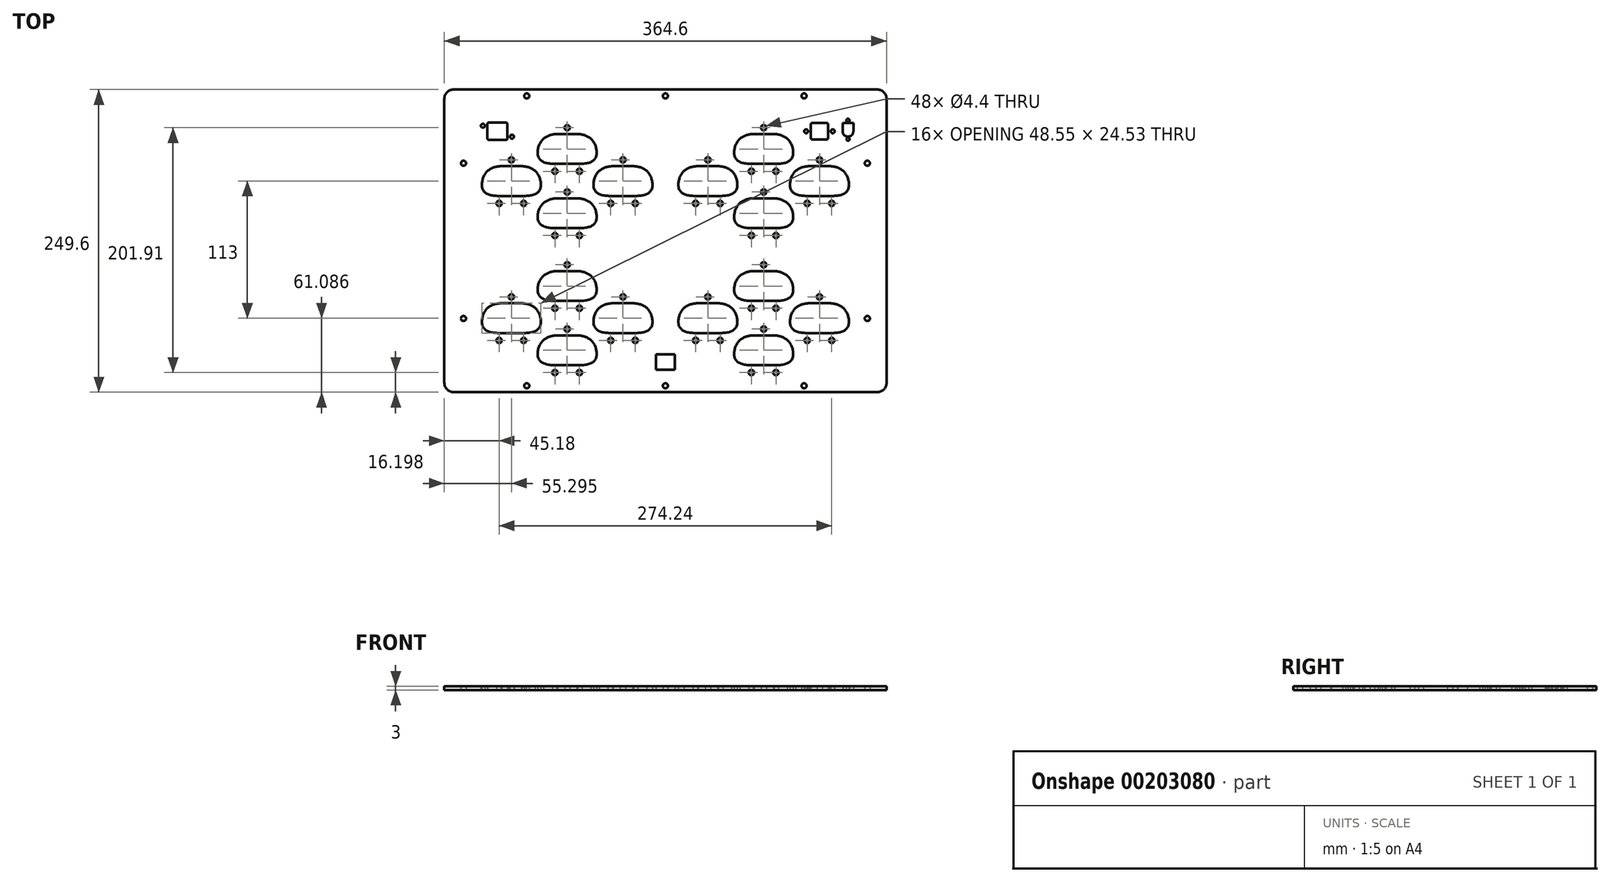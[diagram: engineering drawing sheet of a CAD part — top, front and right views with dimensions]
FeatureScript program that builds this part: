
annotation { "Feature Type Name" : "Feature", "Feature Type Description" : "" }
export const myFeature = defineFeature(function(context is Context, id is Id, definition is map)
    precondition{}
    {
        {
            var Q0;
            Q0=qCreatedBy(makeId("Top.planeOp"),FACE);
            var sketch = newSketch(context, id + "F0", { "sketchPlane" : qUnion([Q0])});
            skLineSegment(sketch, "E0.bottom", {"start": v(-174.5, 124.8) * mm, "end": v(174.5, 124.8) * mm});
            skLineSegment(sketch, "E0.top", {"start": v(-174.5, -124.8) * mm, "end": v(174.5, -124.8) * mm});
            skLineSegment(sketch, "E0.left", {"start": v(-182.3, 117) * mm, "end": v(-182.3, -117) * mm});
            skLineSegment(sketch, "E0.right", {"start": v(182.3, 117) * mm, "end": v(182.3, -117) * mm});
            skPoint(sketch, "E1.visualSharp", {"position": v(-182.3, 124.8) * mm});
            skArc(sketch, "E1.filletArc", {"start": v(-174.5, 124.8) * mm, "mid": v(-180.02, 122.52) * mm, "end": v(-182.3, 117) * mm});
            skPoint(sketch, "E2.visualSharp", {"position": v(182.3, 124.8) * mm});
            skArc(sketch, "E2.filletArc", {"start": v(182.3, 117) * mm, "mid": v(180.02, 122.52) * mm, "end": v(174.5, 124.8) * mm});
            skPoint(sketch, "E3.visualSharp", {"position": v(182.3, -124.8) * mm});
            skArc(sketch, "E3.filletArc", {"start": v(174.5, -124.8) * mm, "mid": v(180.02, -122.52) * mm, "end": v(182.3, -117) * mm});
            skPoint(sketch, "E4.visualSharp", {"position": v(-182.3, -124.8) * mm});
            skArc(sketch, "E4.filletArc", {"start": v(-182.3, -117) * mm, "mid": v(-180.02, -122.52) * mm, "end": v(-174.5, -124.8) * mm});
            skCircle(sketch, "E5", {"center": v(-166.5, -64) * mm, "radius": 2.1 * mm});
            skCircle(sketch, "E6", {"center": v(-166.5, 64) * mm, "radius": 2.1 * mm});
            skCircle(sketch, "E7.MirrorC", {"center": v(166.5, 64) * mm, "radius": 2.1 * mm});
            skCircle(sketch, "E8.MirrorC", {"center": v(166.5, -64) * mm, "radius": 2.1 * mm});
            skCircle(sketch, "E9", {"center": v(-114.33, -119.5) * mm, "radius": 2.1 * mm});
            skCircle(sketch, "E10", {"center": v(0, -119.5) * mm, "radius": 2.1 * mm});
            skCircle(sketch, "E11.MirrorC", {"center": v(114.33, -119.5) * mm, "radius": 2.1 * mm});
            skCircle(sketch, "E12.MirrorC", {"center": v(-114.33, 119.5) * mm, "radius": 2.1 * mm});
            skCircle(sketch, "E13.MirrorC", {"center": v(0, 119.5) * mm, "radius": 2.1 * mm});
            skCircle(sketch, "E14.MirrorC", {"center": v(114.33, 119.5) * mm, "radius": 2.1 * mm});
            skLineSegment(sketch, "E15.1", {"start": v(-135.12, -51.46) * mm, "end": v(-118.9, -51.46) * mm});
            skLineSegment(sketch, "E15.3", {"start": v(-118.9, -51.46) * mm, "end": v(-118.33, -51.45) * mm});
            skArc(sketch, "E15.4", {"start": v(-118.33, -51.45) * mm, "mid": v(-112.6, -52.41) * mm, "end": v(-107.49, -55.2) * mm});
            skArc(sketch, "E15.5", {"start": v(-107.49, -55.2) * mm, "mid": v(-103.73, -60.96) * mm, "end": v(-102.78, -67.78) * mm});
            skLineSegment(sketch, "E15.8", {"start": v(-135.1, -75.97) * mm, "end": v(-118.9, -75.97) * mm});
            skFitSpline(sketch, "E15.9", {"points": [v(-102.78, -67.78) * mm, v(-102.83, -68.48) * mm, v(-103.13, -69.85) * mm, v(-104.12, -71.74) * mm, v(-105.36, -73.07) * mm, v(-106.59, -73.94) * mm, v(-107.95, -74.65) * mm, v(-109.89, -75.3) * mm, v(-112.56, -75.75) * mm, v(-115.56, -75.96) * mm, v(-117.76, -75.98) * mm, v(-118.9, -75.97) * mm]});
            skCircle(sketch, "E16", {"center": v(-127, -46.2) * mm, "radius": 2.2 * mm});
            skCircle(sketch, "E17", {"center": v(-137.12, -82.1) * mm, "radius": 2.2 * mm});
            skCircle(sketch, "E18", {"center": v(-116.88, -82.1) * mm, "radius": 2.2 * mm});
            skFitSpline(sketch, "E19.0", {"points": [v(-151.23, -67.78) * mm, v(-151.18, -68.48) * mm, v(-150.87, -69.85) * mm, v(-149.88, -71.74) * mm, v(-148.63, -73.07) * mm, v(-147.4, -73.93) * mm, v(-146.05, -74.65) * mm, v(-144.11, -75.3) * mm, v(-141.44, -75.75) * mm, v(-138.45, -75.95) * mm, v(-136.25, -75.98) * mm, v(-135.1, -75.97) * mm]});
            skArc(sketch, "E19.1", {"start": v(-146.52, -55.2) * mm, "mid": v(-150.28, -60.96) * mm, "end": v(-151.23, -67.78) * mm});
            skArc(sketch, "E19.2", {"start": v(-135.66, -51.45) * mm, "mid": v(-141.4, -52.41) * mm, "end": v(-146.52, -55.2) * mm});
            skLineSegment(sketch, "E20.0", {"start": v(-135.1, -51.46) * mm, "end": v(-135.66, -51.45) * mm});
            skPoint(sketch, "E21", {"position": v(-156, -112.5) * mm});
            skLineSegment(sketch, "E22.1", {"start": v(-89.12, -77.96) * mm, "end": v(-72.9, -77.96) * mm});
            skLineSegment(sketch, "E22.3", {"start": v(-72.9, -77.96) * mm, "end": v(-72.33, -77.95) * mm});
            skArc(sketch, "E22.4", {"start": v(-72.33, -77.95) * mm, "mid": v(-66.6, -78.91) * mm, "end": v(-61.49, -81.7) * mm});
            skArc(sketch, "E22.5", {"start": v(-61.49, -81.7) * mm, "mid": v(-57.73, -87.46) * mm, "end": v(-56.78, -94.28) * mm});
            skLineSegment(sketch, "E22.8", {"start": v(-89.1, -102.47) * mm, "end": v(-72.9, -102.47) * mm});
            skFitSpline(sketch, "E22.9", {"points": [v(-56.78, -94.28) * mm, v(-56.83, -94.98) * mm, v(-57.13, -96.35) * mm, v(-58.12, -98.24) * mm, v(-59.36, -99.57) * mm, v(-60.58, -100.44) * mm, v(-61.95, -101.15) * mm, v(-63.88, -101.8) * mm, v(-66.56, -102.25) * mm, v(-69.56, -102.45) * mm, v(-71.76, -102.48) * mm, v(-72.9, -102.47) * mm]});
            skCircle(sketch, "E23", {"center": v(-81, -72.7) * mm, "radius": 2.2 * mm});
            skCircle(sketch, "E24", {"center": v(-91.12, -108.6) * mm, "radius": 2.2 * mm});
            skCircle(sketch, "E25", {"center": v(-70.88, -108.6) * mm, "radius": 2.2 * mm});
            skFitSpline(sketch, "E26.0", {"points": [v(-105.23, -94.28) * mm, v(-105.18, -94.98) * mm, v(-104.87, -96.35) * mm, v(-103.88, -98.24) * mm, v(-102.63, -99.57) * mm, v(-101.4, -100.43) * mm, v(-100.05, -101.15) * mm, v(-98.11, -101.8) * mm, v(-95.44, -102.25) * mm, v(-92.45, -102.45) * mm, v(-90.25, -102.48) * mm, v(-89.1, -102.47) * mm]});
            skArc(sketch, "E26.1", {"start": v(-100.52, -81.7) * mm, "mid": v(-104.28, -87.46) * mm, "end": v(-105.23, -94.28) * mm});
            skArc(sketch, "E26.2", {"start": v(-89.66, -77.95) * mm, "mid": v(-95.4, -78.91) * mm, "end": v(-100.52, -81.7) * mm});
            skLineSegment(sketch, "E27.0", {"start": v(-89.1, -77.96) * mm, "end": v(-89.66, -77.95) * mm});
            skLineSegment(sketch, "E28.1", {"start": v(-43.12, -51.46) * mm, "end": v(-26.9, -51.46) * mm});
            skLineSegment(sketch, "E28.3", {"start": v(-26.9, -51.46) * mm, "end": v(-26.33, -51.45) * mm});
            skArc(sketch, "E28.4", {"start": v(-26.33, -51.45) * mm, "mid": v(-20.6, -52.41) * mm, "end": v(-15.49, -55.2) * mm});
            skArc(sketch, "E28.5", {"start": v(-15.49, -55.2) * mm, "mid": v(-11.73, -60.96) * mm, "end": v(-10.78, -67.78) * mm});
            skLineSegment(sketch, "E28.8", {"start": v(-43.1, -75.97) * mm, "end": v(-26.9, -75.97) * mm});
            skFitSpline(sketch, "E28.9", {"points": [v(-10.78, -67.78) * mm, v(-10.83, -68.48) * mm, v(-11.13, -69.85) * mm, v(-12.12, -71.74) * mm, v(-13.36, -73.07) * mm, v(-14.59, -73.94) * mm, v(-15.95, -74.65) * mm, v(-17.89, -75.3) * mm, v(-20.56, -75.75) * mm, v(-23.56, -75.96) * mm, v(-25.76, -75.98) * mm, v(-26.9, -75.97) * mm]});
            skCircle(sketch, "E29", {"center": v(-35, -46.2) * mm, "radius": 2.2 * mm});
            skCircle(sketch, "E30", {"center": v(-45.12, -82.1) * mm, "radius": 2.2 * mm});
            skCircle(sketch, "E31", {"center": v(-24.88, -82.1) * mm, "radius": 2.2 * mm});
            skFitSpline(sketch, "E32.0", {"points": [v(-59.23, -67.78) * mm, v(-59.18, -68.48) * mm, v(-58.87, -69.85) * mm, v(-57.88, -71.74) * mm, v(-56.63, -73.07) * mm, v(-55.4, -73.93) * mm, v(-54.05, -74.65) * mm, v(-52.11, -75.3) * mm, v(-49.44, -75.75) * mm, v(-46.45, -75.95) * mm, v(-44.25, -75.98) * mm, v(-43.1, -75.97) * mm]});
            skArc(sketch, "E32.1", {"start": v(-54.52, -55.2) * mm, "mid": v(-58.28, -60.96) * mm, "end": v(-59.23, -67.78) * mm});
            skArc(sketch, "E32.2", {"start": v(-43.66, -51.45) * mm, "mid": v(-49.4, -52.41) * mm, "end": v(-54.52, -55.2) * mm});
            skLineSegment(sketch, "E33.0", {"start": v(-43.1, -51.46) * mm, "end": v(-43.66, -51.45) * mm});
            skLineSegment(sketch, "E34.1", {"start": v(-89.12, -24.96) * mm, "end": v(-72.9, -24.96) * mm});
            skLineSegment(sketch, "E34.3", {"start": v(-72.9, -24.96) * mm, "end": v(-72.33, -24.95) * mm});
            skArc(sketch, "E34.4", {"start": v(-72.33, -24.95) * mm, "mid": v(-66.6, -25.91) * mm, "end": v(-61.49, -28.7) * mm});
            skArc(sketch, "E34.5", {"start": v(-61.49, -28.7) * mm, "mid": v(-57.73, -34.46) * mm, "end": v(-56.78, -41.28) * mm});
            skLineSegment(sketch, "E34.8", {"start": v(-89.1, -49.47) * mm, "end": v(-72.9, -49.47) * mm});
            skFitSpline(sketch, "E34.9", {"points": [v(-56.78, -41.28) * mm, v(-56.83, -41.98) * mm, v(-57.13, -43.35) * mm, v(-58.12, -45.24) * mm, v(-59.36, -46.57) * mm, v(-60.59, -47.44) * mm, v(-61.95, -48.15) * mm, v(-63.89, -48.8) * mm, v(-66.56, -49.25) * mm, v(-69.56, -49.46) * mm, v(-71.76, -49.48) * mm, v(-72.9, -49.47) * mm]});
            skCircle(sketch, "E35", {"center": v(-81, -19.7) * mm, "radius": 2.2 * mm});
            skCircle(sketch, "E36", {"center": v(-91.12, -55.6) * mm, "radius": 2.2 * mm});
            skCircle(sketch, "E37", {"center": v(-70.88, -55.6) * mm, "radius": 2.2 * mm});
            skFitSpline(sketch, "E38.0", {"points": [v(-105.23, -41.28) * mm, v(-105.18, -41.98) * mm, v(-104.87, -43.35) * mm, v(-103.88, -45.24) * mm, v(-102.63, -46.57) * mm, v(-101.4, -47.43) * mm, v(-100.05, -48.15) * mm, v(-98.11, -48.8) * mm, v(-95.44, -49.25) * mm, v(-92.45, -49.45) * mm, v(-90.25, -49.48) * mm, v(-89.1, -49.47) * mm]});
            skArc(sketch, "E38.1", {"start": v(-100.52, -28.7) * mm, "mid": v(-104.28, -34.46) * mm, "end": v(-105.23, -41.28) * mm});
            skArc(sketch, "E38.2", {"start": v(-89.66, -24.95) * mm, "mid": v(-95.4, -25.91) * mm, "end": v(-100.52, -28.7) * mm});
            skLineSegment(sketch, "E39.0", {"start": v(-89.1, -24.96) * mm, "end": v(-89.66, -24.95) * mm});
            skLineSegment(sketch, "E40.1", {"start": v(-135.12, 61.54) * mm, "end": v(-118.9, 61.54) * mm});
            skLineSegment(sketch, "E40.3", {"start": v(-118.9, 61.54) * mm, "end": v(-118.33, 61.55) * mm});
            skArc(sketch, "E40.4", {"start": v(-118.33, 61.55) * mm, "mid": v(-112.6, 60.59) * mm, "end": v(-107.49, 57.8) * mm});
            skArc(sketch, "E40.5", {"start": v(-107.49, 57.8) * mm, "mid": v(-103.73, 52.04) * mm, "end": v(-102.78, 45.22) * mm});
            skLineSegment(sketch, "E40.8", {"start": v(-135.1, 37.03) * mm, "end": v(-118.9, 37.03) * mm});
            skFitSpline(sketch, "E40.9", {"points": [v(-102.78, 45.22) * mm, v(-102.83, 44.52) * mm, v(-103.13, 43.15) * mm, v(-104.12, 41.26) * mm, v(-105.36, 39.93) * mm, v(-106.59, 39.06) * mm, v(-107.95, 38.35) * mm, v(-109.89, 37.7) * mm, v(-112.56, 37.25) * mm, v(-115.56, 37.04) * mm, v(-117.76, 37.02) * mm, v(-118.9, 37.03) * mm]});
            skCircle(sketch, "E41", {"center": v(-127, 66.8) * mm, "radius": 2.2 * mm});
            skCircle(sketch, "E42", {"center": v(-137.12, 30.9) * mm, "radius": 2.2 * mm});
            skCircle(sketch, "E43", {"center": v(-116.88, 30.9) * mm, "radius": 2.2 * mm});
            skFitSpline(sketch, "E44.0", {"points": [v(-151.23, 45.22) * mm, v(-151.18, 44.52) * mm, v(-150.87, 43.15) * mm, v(-149.88, 41.26) * mm, v(-148.63, 39.93) * mm, v(-147.4, 39.07) * mm, v(-146.05, 38.35) * mm, v(-144.11, 37.7) * mm, v(-141.44, 37.25) * mm, v(-138.45, 37.05) * mm, v(-136.25, 37.02) * mm, v(-135.1, 37.03) * mm]});
            skArc(sketch, "E44.1", {"start": v(-146.52, 57.8) * mm, "mid": v(-150.28, 52.04) * mm, "end": v(-151.23, 45.22) * mm});
            skArc(sketch, "E44.2", {"start": v(-135.66, 61.55) * mm, "mid": v(-141.4, 60.59) * mm, "end": v(-146.52, 57.8) * mm});
            skLineSegment(sketch, "E45.0", {"start": v(-135.1, 61.54) * mm, "end": v(-135.66, 61.55) * mm});
            skLineSegment(sketch, "E46.1", {"start": v(-89.12, 35.04) * mm, "end": v(-72.9, 35.04) * mm});
            skLineSegment(sketch, "E46.3", {"start": v(-72.9, 35.04) * mm, "end": v(-72.33, 35.05) * mm});
            skArc(sketch, "E46.4", {"start": v(-72.33, 35.05) * mm, "mid": v(-66.6, 34.09) * mm, "end": v(-61.49, 31.3) * mm});
            skArc(sketch, "E46.5", {"start": v(-61.49, 31.3) * mm, "mid": v(-57.73, 25.54) * mm, "end": v(-56.78, 18.72) * mm});
            skLineSegment(sketch, "E46.8", {"start": v(-89.1, 10.53) * mm, "end": v(-72.9, 10.53) * mm});
            skFitSpline(sketch, "E46.9", {"points": [v(-56.78, 18.72) * mm, v(-56.83, 18.02) * mm, v(-57.13, 16.65) * mm, v(-58.12, 14.76) * mm, v(-59.36, 13.43) * mm, v(-60.59, 12.56) * mm, v(-61.95, 11.85) * mm, v(-63.89, 11.2) * mm, v(-66.56, 10.75) * mm, v(-69.56, 10.54) * mm, v(-71.76, 10.52) * mm, v(-72.9, 10.53) * mm]});
            skCircle(sketch, "E47", {"center": v(-81, 40.3) * mm, "radius": 2.2 * mm});
            skCircle(sketch, "E48", {"center": v(-91.12, 4.4) * mm, "radius": 2.2 * mm});
            skCircle(sketch, "E49", {"center": v(-70.88, 4.4) * mm, "radius": 2.2 * mm});
            skFitSpline(sketch, "E50.0", {"points": [v(-105.23, 18.72) * mm, v(-105.18, 18.02) * mm, v(-104.87, 16.65) * mm, v(-103.88, 14.76) * mm, v(-102.63, 13.43) * mm, v(-101.4, 12.57) * mm, v(-100.05, 11.85) * mm, v(-98.11, 11.2) * mm, v(-95.44, 10.75) * mm, v(-92.45, 10.55) * mm, v(-90.25, 10.52) * mm, v(-89.1, 10.53) * mm]});
            skArc(sketch, "E50.1", {"start": v(-100.52, 31.3) * mm, "mid": v(-104.28, 25.54) * mm, "end": v(-105.23, 18.72) * mm});
            skArc(sketch, "E50.2", {"start": v(-89.66, 35.05) * mm, "mid": v(-95.4, 34.09) * mm, "end": v(-100.52, 31.3) * mm});
            skLineSegment(sketch, "E51.0", {"start": v(-89.1, 35.04) * mm, "end": v(-89.66, 35.05) * mm});
            skLineSegment(sketch, "E52.1", {"start": v(-43.12, 61.54) * mm, "end": v(-26.9, 61.54) * mm});
            skLineSegment(sketch, "E52.3", {"start": v(-26.9, 61.54) * mm, "end": v(-26.33, 61.55) * mm});
            skArc(sketch, "E52.4", {"start": v(-26.33, 61.55) * mm, "mid": v(-20.6, 60.59) * mm, "end": v(-15.49, 57.8) * mm});
            skArc(sketch, "E52.5", {"start": v(-15.49, 57.8) * mm, "mid": v(-11.73, 52.04) * mm, "end": v(-10.77, 45.22) * mm});
            skLineSegment(sketch, "E52.8", {"start": v(-43.1, 37.03) * mm, "end": v(-26.9, 37.03) * mm});
            skFitSpline(sketch, "E52.9", {"points": [v(-10.77, 45.22) * mm, v(-10.83, 44.52) * mm, v(-11.13, 43.15) * mm, v(-12.12, 41.26) * mm, v(-13.36, 39.93) * mm, v(-14.58, 39.06) * mm, v(-15.95, 38.35) * mm, v(-17.88, 37.7) * mm, v(-20.56, 37.25) * mm, v(-23.56, 37.04) * mm, v(-25.76, 37.02) * mm, v(-26.9, 37.03) * mm]});
            skCircle(sketch, "E53", {"center": v(-35, 66.8) * mm, "radius": 2.2 * mm});
            skCircle(sketch, "E54", {"center": v(-45.12, 30.9) * mm, "radius": 2.2 * mm});
            skCircle(sketch, "E55", {"center": v(-24.88, 30.9) * mm, "radius": 2.2 * mm});
            skFitSpline(sketch, "E56.0", {"points": [v(-59.23, 45.22) * mm, v(-59.18, 44.52) * mm, v(-58.87, 43.15) * mm, v(-57.88, 41.27) * mm, v(-56.63, 39.93) * mm, v(-55.4, 39.07) * mm, v(-54.05, 38.35) * mm, v(-52.11, 37.7) * mm, v(-49.44, 37.26) * mm, v(-46.45, 37.05) * mm, v(-44.25, 37.02) * mm, v(-43.1, 37.03) * mm]});
            skArc(sketch, "E56.1", {"start": v(-54.52, 57.8) * mm, "mid": v(-58.28, 52.03) * mm, "end": v(-59.23, 45.22) * mm});
            skArc(sketch, "E56.2", {"start": v(-43.66, 61.55) * mm, "mid": v(-49.4, 60.59) * mm, "end": v(-54.52, 57.8) * mm});
            skLineSegment(sketch, "E57.0", {"start": v(-43.1, 61.54) * mm, "end": v(-43.66, 61.55) * mm});
            skLineSegment(sketch, "E58.1", {"start": v(-89.12, 88.04) * mm, "end": v(-72.9, 88.04) * mm});
            skLineSegment(sketch, "E58.3", {"start": v(-72.9, 88.04) * mm, "end": v(-72.33, 88.05) * mm});
            skArc(sketch, "E58.4", {"start": v(-72.33, 88.05) * mm, "mid": v(-66.6, 87.09) * mm, "end": v(-61.49, 84.3) * mm});
            skArc(sketch, "E58.5", {"start": v(-61.49, 84.3) * mm, "mid": v(-57.73, 78.54) * mm, "end": v(-56.78, 71.72) * mm});
            skLineSegment(sketch, "E58.8", {"start": v(-89.1, 63.53) * mm, "end": v(-72.9, 63.53) * mm});
            skFitSpline(sketch, "E58.9", {"points": [v(-56.78, 71.72) * mm, v(-56.83, 71.02) * mm, v(-57.13, 69.65) * mm, v(-58.12, 67.76) * mm, v(-59.36, 66.43) * mm, v(-60.59, 65.56) * mm, v(-61.95, 64.85) * mm, v(-63.89, 64.2) * mm, v(-66.56, 63.75) * mm, v(-69.56, 63.54) * mm, v(-71.76, 63.52) * mm, v(-72.9, 63.53) * mm]});
            skCircle(sketch, "E59", {"center": v(-81, 93.3) * mm, "radius": 2.2 * mm});
            skCircle(sketch, "E60", {"center": v(-91.12, 57.4) * mm, "radius": 2.2 * mm});
            skCircle(sketch, "E61", {"center": v(-70.88, 57.4) * mm, "radius": 2.2 * mm});
            skFitSpline(sketch, "E62.0", {"points": [v(-105.23, 71.72) * mm, v(-105.18, 71.02) * mm, v(-104.87, 69.65) * mm, v(-103.88, 67.76) * mm, v(-102.63, 66.43) * mm, v(-101.4, 65.57) * mm, v(-100.05, 64.85) * mm, v(-98.11, 64.2) * mm, v(-95.44, 63.75) * mm, v(-92.45, 63.55) * mm, v(-90.25, 63.52) * mm, v(-89.1, 63.53) * mm]});
            skArc(sketch, "E62.1", {"start": v(-100.52, 84.3) * mm, "mid": v(-104.28, 78.54) * mm, "end": v(-105.23, 71.72) * mm});
            skArc(sketch, "E62.2", {"start": v(-89.66, 88.05) * mm, "mid": v(-95.4, 87.09) * mm, "end": v(-100.52, 84.3) * mm});
            skLineSegment(sketch, "E63.0", {"start": v(-89.1, 88.04) * mm, "end": v(-89.66, 88.05) * mm});
            skLineSegment(sketch, "E64.1", {"start": v(26.88, 61.54) * mm, "end": v(43.1, 61.54) * mm});
            skLineSegment(sketch, "E64.3", {"start": v(43.1, 61.54) * mm, "end": v(43.67, 61.55) * mm});
            skArc(sketch, "E64.4", {"start": v(43.67, 61.55) * mm, "mid": v(49.4, 60.59) * mm, "end": v(54.51, 57.8) * mm});
            skArc(sketch, "E64.5", {"start": v(54.51, 57.8) * mm, "mid": v(58.27, 52.04) * mm, "end": v(59.22, 45.22) * mm});
            skLineSegment(sketch, "E64.8", {"start": v(26.9, 37.03) * mm, "end": v(43.1, 37.03) * mm});
            skFitSpline(sketch, "E64.9", {"points": [v(59.22, 45.22) * mm, v(59.17, 44.52) * mm, v(58.87, 43.15) * mm, v(57.88, 41.26) * mm, v(56.64, 39.93) * mm, v(55.42, 39.06) * mm, v(54.05, 38.35) * mm, v(52.12, 37.7) * mm, v(49.44, 37.25) * mm, v(46.44, 37.05) * mm, v(44.24, 37.02) * mm, v(43.1, 37.03) * mm]});
            skCircle(sketch, "E65", {"center": v(35, 66.8) * mm, "radius": 2.2 * mm});
            skCircle(sketch, "E66", {"center": v(24.88, 30.9) * mm, "radius": 2.2 * mm});
            skCircle(sketch, "E67", {"center": v(45.12, 30.9) * mm, "radius": 2.2 * mm});
            skFitSpline(sketch, "E68.0", {"points": [v(10.77, 45.22) * mm, v(10.82, 44.52) * mm, v(11.13, 43.15) * mm, v(12.12, 41.26) * mm, v(13.37, 39.93) * mm, v(14.6, 39.07) * mm, v(15.95, 38.35) * mm, v(17.89, 37.7) * mm, v(20.56, 37.25) * mm, v(23.55, 37.05) * mm, v(25.75, 37.02) * mm, v(26.9, 37.03) * mm]});
            skArc(sketch, "E68.1", {"start": v(15.48, 57.8) * mm, "mid": v(11.72, 52.04) * mm, "end": v(10.77, 45.22) * mm});
            skArc(sketch, "E68.2", {"start": v(26.34, 61.55) * mm, "mid": v(20.6, 60.59) * mm, "end": v(15.48, 57.8) * mm});
            skLineSegment(sketch, "E69.0", {"start": v(26.9, 61.54) * mm, "end": v(26.34, 61.55) * mm});
            skLineSegment(sketch, "E70.1", {"start": v(72.88, 35.04) * mm, "end": v(89.1, 35.04) * mm});
            skLineSegment(sketch, "E70.3", {"start": v(89.1, 35.04) * mm, "end": v(89.67, 35.05) * mm});
            skArc(sketch, "E70.4", {"start": v(89.67, 35.05) * mm, "mid": v(95.4, 34.09) * mm, "end": v(100.51, 31.3) * mm});
            skArc(sketch, "E70.5", {"start": v(100.51, 31.3) * mm, "mid": v(104.27, 25.54) * mm, "end": v(105.22, 18.72) * mm});
            skLineSegment(sketch, "E70.8", {"start": v(72.9, 10.53) * mm, "end": v(89.1, 10.53) * mm});
            skFitSpline(sketch, "E70.9", {"points": [v(105.22, 18.72) * mm, v(105.17, 18.02) * mm, v(104.87, 16.65) * mm, v(103.88, 14.76) * mm, v(102.64, 13.43) * mm, v(101.42, 12.56) * mm, v(100.05, 11.85) * mm, v(98.12, 11.2) * mm, v(95.44, 10.75) * mm, v(92.44, 10.55) * mm, v(90.24, 10.52) * mm, v(89.1, 10.53) * mm]});
            skCircle(sketch, "E71", {"center": v(81, 40.3) * mm, "radius": 2.2 * mm});
            skCircle(sketch, "E72", {"center": v(70.88, 4.4) * mm, "radius": 2.2 * mm});
            skCircle(sketch, "E73", {"center": v(91.12, 4.4) * mm, "radius": 2.2 * mm});
            skFitSpline(sketch, "E74.0", {"points": [v(56.77, 18.72) * mm, v(56.82, 18.02) * mm, v(57.13, 16.65) * mm, v(58.12, 14.76) * mm, v(59.37, 13.43) * mm, v(60.6, 12.57) * mm, v(61.95, 11.85) * mm, v(63.89, 11.2) * mm, v(66.56, 10.75) * mm, v(69.55, 10.55) * mm, v(71.75, 10.52) * mm, v(72.9, 10.53) * mm]});
            skArc(sketch, "E74.1", {"start": v(61.48, 31.3) * mm, "mid": v(57.72, 25.54) * mm, "end": v(56.77, 18.72) * mm});
            skArc(sketch, "E74.2", {"start": v(72.34, 35.05) * mm, "mid": v(66.6, 34.09) * mm, "end": v(61.48, 31.3) * mm});
            skLineSegment(sketch, "E75.0", {"start": v(72.9, 35.04) * mm, "end": v(72.34, 35.05) * mm});
            skLineSegment(sketch, "E76.1", {"start": v(118.88, 61.54) * mm, "end": v(135.1, 61.54) * mm});
            skLineSegment(sketch, "E76.3", {"start": v(135.1, 61.54) * mm, "end": v(135.67, 61.55) * mm});
            skArc(sketch, "E76.4", {"start": v(135.67, 61.55) * mm, "mid": v(141.4, 60.59) * mm, "end": v(146.51, 57.8) * mm});
            skArc(sketch, "E76.5", {"start": v(146.51, 57.8) * mm, "mid": v(150.27, 52.04) * mm, "end": v(151.22, 45.22) * mm});
            skLineSegment(sketch, "E76.8", {"start": v(118.9, 37.03) * mm, "end": v(135.1, 37.03) * mm});
            skFitSpline(sketch, "E76.9", {"points": [v(151.22, 45.22) * mm, v(151.17, 44.52) * mm, v(150.87, 43.15) * mm, v(149.88, 41.26) * mm, v(148.64, 39.93) * mm, v(147.42, 39.06) * mm, v(146.05, 38.35) * mm, v(144.12, 37.7) * mm, v(141.44, 37.25) * mm, v(138.44, 37.05) * mm, v(136.24, 37.02) * mm, v(135.1, 37.03) * mm]});
            skCircle(sketch, "E77", {"center": v(127, 66.8) * mm, "radius": 2.2 * mm});
            skCircle(sketch, "E78", {"center": v(116.88, 30.9) * mm, "radius": 2.2 * mm});
            skCircle(sketch, "E79", {"center": v(137.12, 30.9) * mm, "radius": 2.2 * mm});
            skFitSpline(sketch, "E80.0", {"points": [v(102.77, 45.22) * mm, v(102.82, 44.52) * mm, v(103.13, 43.15) * mm, v(104.12, 41.26) * mm, v(105.37, 39.93) * mm, v(106.6, 39.07) * mm, v(107.95, 38.35) * mm, v(109.89, 37.7) * mm, v(112.56, 37.25) * mm, v(115.55, 37.05) * mm, v(117.75, 37.02) * mm, v(118.9, 37.03) * mm]});
            skArc(sketch, "E80.1", {"start": v(107.48, 57.8) * mm, "mid": v(103.72, 52.04) * mm, "end": v(102.77, 45.22) * mm});
            skArc(sketch, "E80.2", {"start": v(118.34, 61.55) * mm, "mid": v(112.6, 60.59) * mm, "end": v(107.48, 57.8) * mm});
            skLineSegment(sketch, "E81.0", {"start": v(118.9, 61.54) * mm, "end": v(118.34, 61.55) * mm});
            skLineSegment(sketch, "E82.1", {"start": v(72.88, 88.04) * mm, "end": v(89.1, 88.04) * mm});
            skLineSegment(sketch, "E82.3", {"start": v(89.1, 88.04) * mm, "end": v(89.67, 88.05) * mm});
            skArc(sketch, "E82.4", {"start": v(89.67, 88.05) * mm, "mid": v(95.4, 87.09) * mm, "end": v(100.51, 84.3) * mm});
            skArc(sketch, "E82.5", {"start": v(100.51, 84.3) * mm, "mid": v(104.27, 78.54) * mm, "end": v(105.22, 71.72) * mm});
            skLineSegment(sketch, "E82.8", {"start": v(72.9, 63.53) * mm, "end": v(89.1, 63.53) * mm});
            skFitSpline(sketch, "E82.9", {"points": [v(105.22, 71.72) * mm, v(105.17, 71.02) * mm, v(104.87, 69.65) * mm, v(103.88, 67.76) * mm, v(102.64, 66.43) * mm, v(101.42, 65.56) * mm, v(100.05, 64.85) * mm, v(98.12, 64.2) * mm, v(95.44, 63.75) * mm, v(92.44, 63.55) * mm, v(90.24, 63.52) * mm, v(89.1, 63.53) * mm]});
            skCircle(sketch, "E83", {"center": v(81, 93.3) * mm, "radius": 2.2 * mm});
            skCircle(sketch, "E84", {"center": v(70.88, 57.4) * mm, "radius": 2.2 * mm});
            skCircle(sketch, "E85", {"center": v(91.12, 57.4) * mm, "radius": 2.2 * mm});
            skFitSpline(sketch, "E86.0", {"points": [v(56.77, 71.72) * mm, v(56.82, 71.02) * mm, v(57.13, 69.65) * mm, v(58.12, 67.76) * mm, v(59.37, 66.43) * mm, v(60.6, 65.57) * mm, v(61.95, 64.85) * mm, v(63.89, 64.2) * mm, v(66.56, 63.75) * mm, v(69.55, 63.55) * mm, v(71.75, 63.52) * mm, v(72.9, 63.53) * mm]});
            skArc(sketch, "E86.1", {"start": v(61.48, 84.3) * mm, "mid": v(57.72, 78.54) * mm, "end": v(56.77, 71.72) * mm});
            skArc(sketch, "E86.2", {"start": v(72.34, 88.05) * mm, "mid": v(66.6, 87.09) * mm, "end": v(61.48, 84.3) * mm});
            skLineSegment(sketch, "E87.0", {"start": v(72.9, 88.04) * mm, "end": v(72.34, 88.05) * mm});
            skLineSegment(sketch, "E88.1", {"start": v(26.88, -51.46) * mm, "end": v(43.1, -51.46) * mm});
            skLineSegment(sketch, "E88.3", {"start": v(43.1, -51.46) * mm, "end": v(43.67, -51.45) * mm});
            skArc(sketch, "E88.4", {"start": v(43.67, -51.45) * mm, "mid": v(49.4, -52.41) * mm, "end": v(54.51, -55.2) * mm});
            skArc(sketch, "E88.5", {"start": v(54.51, -55.2) * mm, "mid": v(58.27, -60.96) * mm, "end": v(59.22, -67.78) * mm});
            skLineSegment(sketch, "E88.8", {"start": v(26.9, -75.97) * mm, "end": v(43.1, -75.97) * mm});
            skFitSpline(sketch, "E88.9", {"points": [v(59.22, -67.78) * mm, v(59.17, -68.48) * mm, v(58.87, -69.85) * mm, v(57.88, -71.74) * mm, v(56.64, -73.07) * mm, v(55.41, -73.94) * mm, v(54.05, -74.65) * mm, v(52.11, -75.3) * mm, v(49.44, -75.75) * mm, v(46.44, -75.96) * mm, v(44.24, -75.98) * mm, v(43.1, -75.97) * mm]});
            skCircle(sketch, "E89", {"center": v(35, -46.2) * mm, "radius": 2.2 * mm});
            skCircle(sketch, "E90", {"center": v(24.88, -82.1) * mm, "radius": 2.2 * mm});
            skCircle(sketch, "E91", {"center": v(45.12, -82.1) * mm, "radius": 2.2 * mm});
            skFitSpline(sketch, "E92.0", {"points": [v(10.77, -67.78) * mm, v(10.82, -68.48) * mm, v(11.13, -69.85) * mm, v(12.12, -71.74) * mm, v(13.37, -73.07) * mm, v(14.6, -73.93) * mm, v(15.95, -74.65) * mm, v(17.89, -75.3) * mm, v(20.56, -75.75) * mm, v(23.55, -75.95) * mm, v(25.75, -75.98) * mm, v(26.9, -75.97) * mm]});
            skArc(sketch, "E92.1", {"start": v(15.48, -55.2) * mm, "mid": v(11.72, -60.96) * mm, "end": v(10.77, -67.78) * mm});
            skArc(sketch, "E92.2", {"start": v(26.34, -51.45) * mm, "mid": v(20.6, -52.41) * mm, "end": v(15.48, -55.2) * mm});
            skLineSegment(sketch, "E93.0", {"start": v(26.9, -51.46) * mm, "end": v(26.34, -51.45) * mm});
            skLineSegment(sketch, "E94.1", {"start": v(72.88, -77.96) * mm, "end": v(89.1, -77.96) * mm});
            skLineSegment(sketch, "E94.3", {"start": v(89.1, -77.96) * mm, "end": v(89.67, -77.95) * mm});
            skArc(sketch, "E94.4", {"start": v(89.67, -77.95) * mm, "mid": v(95.4, -78.91) * mm, "end": v(100.51, -81.7) * mm});
            skArc(sketch, "E94.5", {"start": v(100.51, -81.7) * mm, "mid": v(104.27, -87.46) * mm, "end": v(105.22, -94.28) * mm});
            skLineSegment(sketch, "E94.8", {"start": v(72.9, -102.47) * mm, "end": v(89.1, -102.47) * mm});
            skFitSpline(sketch, "E94.9", {"points": [v(105.22, -94.28) * mm, v(105.17, -94.98) * mm, v(104.87, -96.35) * mm, v(103.88, -98.24) * mm, v(102.64, -99.57) * mm, v(101.41, -100.44) * mm, v(100.05, -101.15) * mm, v(98.11, -101.8) * mm, v(95.44, -102.25) * mm, v(92.44, -102.46) * mm, v(90.24, -102.48) * mm, v(89.1, -102.47) * mm]});
            skCircle(sketch, "E95", {"center": v(81, -72.7) * mm, "radius": 2.2 * mm});
            skCircle(sketch, "E96", {"center": v(70.88, -108.6) * mm, "radius": 2.2 * mm});
            skCircle(sketch, "E97", {"center": v(91.12, -108.6) * mm, "radius": 2.2 * mm});
            skFitSpline(sketch, "E98.0", {"points": [v(56.77, -94.28) * mm, v(56.82, -94.98) * mm, v(57.13, -96.35) * mm, v(58.12, -98.24) * mm, v(59.37, -99.57) * mm, v(60.6, -100.43) * mm, v(61.95, -101.15) * mm, v(63.89, -101.8) * mm, v(66.56, -102.25) * mm, v(69.55, -102.45) * mm, v(71.75, -102.48) * mm, v(72.9, -102.47) * mm]});
            skArc(sketch, "E98.1", {"start": v(61.48, -81.7) * mm, "mid": v(57.72, -87.46) * mm, "end": v(56.77, -94.28) * mm});
            skArc(sketch, "E98.2", {"start": v(72.34, -77.95) * mm, "mid": v(66.6, -78.91) * mm, "end": v(61.48, -81.7) * mm});
            skLineSegment(sketch, "E99.0", {"start": v(72.9, -77.96) * mm, "end": v(72.34, -77.95) * mm});
            skLineSegment(sketch, "E100.1", {"start": v(118.88, -51.46) * mm, "end": v(135.1, -51.46) * mm});
            skLineSegment(sketch, "E100.3", {"start": v(135.1, -51.46) * mm, "end": v(135.67, -51.45) * mm});
            skArc(sketch, "E100.4", {"start": v(135.67, -51.45) * mm, "mid": v(141.4, -52.41) * mm, "end": v(146.51, -55.2) * mm});
            skArc(sketch, "E100.5", {"start": v(146.51, -55.2) * mm, "mid": v(150.27, -60.96) * mm, "end": v(151.22, -67.78) * mm});
            skLineSegment(sketch, "E100.8", {"start": v(118.9, -75.97) * mm, "end": v(135.1, -75.97) * mm});
            skFitSpline(sketch, "E100.9", {"points": [v(151.22, -67.78) * mm, v(151.17, -68.48) * mm, v(150.87, -69.85) * mm, v(149.88, -71.74) * mm, v(148.64, -73.07) * mm, v(147.41, -73.94) * mm, v(146.05, -74.65) * mm, v(144.11, -75.3) * mm, v(141.44, -75.75) * mm, v(138.44, -75.96) * mm, v(136.24, -75.98) * mm, v(135.1, -75.97) * mm]});
            skCircle(sketch, "E101", {"center": v(127, -46.2) * mm, "radius": 2.2 * mm});
            skCircle(sketch, "E102", {"center": v(116.88, -82.1) * mm, "radius": 2.2 * mm});
            skCircle(sketch, "E103", {"center": v(137.12, -82.1) * mm, "radius": 2.2 * mm});
            skFitSpline(sketch, "E104.0", {"points": [v(102.77, -67.78) * mm, v(102.82, -68.48) * mm, v(103.13, -69.85) * mm, v(104.12, -71.74) * mm, v(105.37, -73.07) * mm, v(106.6, -73.93) * mm, v(107.95, -74.65) * mm, v(109.89, -75.3) * mm, v(112.56, -75.75) * mm, v(115.55, -75.95) * mm, v(117.75, -75.98) * mm, v(118.9, -75.97) * mm]});
            skArc(sketch, "E104.1", {"start": v(107.48, -55.2) * mm, "mid": v(103.72, -60.96) * mm, "end": v(102.77, -67.78) * mm});
            skArc(sketch, "E104.2", {"start": v(118.34, -51.45) * mm, "mid": v(112.6, -52.41) * mm, "end": v(107.48, -55.2) * mm});
            skLineSegment(sketch, "E105.0", {"start": v(118.9, -51.46) * mm, "end": v(118.34, -51.45) * mm});
            skLineSegment(sketch, "E106.1", {"start": v(72.88, -24.96) * mm, "end": v(89.1, -24.96) * mm});
            skLineSegment(sketch, "E106.3", {"start": v(89.1, -24.96) * mm, "end": v(89.67, -24.95) * mm});
            skArc(sketch, "E106.4", {"start": v(89.67, -24.95) * mm, "mid": v(95.4, -25.91) * mm, "end": v(100.51, -28.7) * mm});
            skArc(sketch, "E106.5", {"start": v(100.51, -28.7) * mm, "mid": v(104.27, -34.46) * mm, "end": v(105.22, -41.28) * mm});
            skLineSegment(sketch, "E106.8", {"start": v(72.9, -49.47) * mm, "end": v(89.1, -49.47) * mm});
            skFitSpline(sketch, "E106.9", {"points": [v(105.22, -41.28) * mm, v(105.17, -41.98) * mm, v(104.87, -43.35) * mm, v(103.88, -45.24) * mm, v(102.64, -46.57) * mm, v(101.41, -47.44) * mm, v(100.05, -48.15) * mm, v(98.11, -48.8) * mm, v(95.44, -49.25) * mm, v(92.44, -49.46) * mm, v(90.24, -49.48) * mm, v(89.1, -49.47) * mm]});
            skCircle(sketch, "E107", {"center": v(81, -19.7) * mm, "radius": 2.2 * mm});
            skCircle(sketch, "E108", {"center": v(70.88, -55.6) * mm, "radius": 2.2 * mm});
            skCircle(sketch, "E109", {"center": v(91.12, -55.6) * mm, "radius": 2.2 * mm});
            skFitSpline(sketch, "E110.0", {"points": [v(56.77, -41.28) * mm, v(56.82, -41.98) * mm, v(57.13, -43.35) * mm, v(58.12, -45.24) * mm, v(59.37, -46.57) * mm, v(60.6, -47.43) * mm, v(61.95, -48.15) * mm, v(63.89, -48.8) * mm, v(66.56, -49.25) * mm, v(69.55, -49.45) * mm, v(71.75, -49.48) * mm, v(72.9, -49.47) * mm]});
            skArc(sketch, "E110.1", {"start": v(61.48, -28.7) * mm, "mid": v(57.72, -34.46) * mm, "end": v(56.77, -41.28) * mm});
            skArc(sketch, "E110.2", {"start": v(72.34, -24.95) * mm, "mid": v(66.6, -25.91) * mm, "end": v(61.48, -28.7) * mm});
            skLineSegment(sketch, "E111.0", {"start": v(72.9, -24.96) * mm, "end": v(72.34, -24.95) * mm});
            skCircle(sketch, "E112", {"center": v(-150.5, 94.9) * mm, "radius": 1.63 * mm});
            skCircle(sketch, "E113", {"center": v(-126.5, 85.9) * mm, "radius": 1.63 * mm});
            skLineSegment(sketch, "E114.bottom", {"start": v(-145.4, 97.67) * mm, "end": v(-131.6, 97.67) * mm});
            skLineSegment(sketch, "E114.top", {"start": v(-145.4, 83.12) * mm, "end": v(-131.6, 83.12) * mm});
            skLineSegment(sketch, "E114.left", {"start": v(-146.78, 96.3) * mm, "end": v(-146.78, 84.5) * mm});
            skLineSegment(sketch, "E114.right", {"start": v(-130.23, 96.3) * mm, "end": v(-130.23, 84.5) * mm});
            skPoint(sketch, "E115.visualSharp", {"position": v(-146.78, 97.67) * mm});
            skArc(sketch, "E115.filletArc", {"start": v(-145.4, 97.67) * mm, "mid": v(-146.37, 97.27) * mm, "end": v(-146.78, 96.3) * mm});
            skPoint(sketch, "E116.visualSharp", {"position": v(-130.23, 97.67) * mm});
            skArc(sketch, "E116.filletArc", {"start": v(-130.23, 96.3) * mm, "mid": v(-130.63, 97.27) * mm, "end": v(-131.6, 97.67) * mm});
            skPoint(sketch, "E117.visualSharp", {"position": v(-130.23, 83.12) * mm});
            skArc(sketch, "E117.filletArc", {"start": v(-131.6, 83.12) * mm, "mid": v(-130.63, 83.53) * mm, "end": v(-130.23, 84.5) * mm});
            skPoint(sketch, "E118.visualSharp", {"position": v(-146.78, 83.12) * mm});
            skArc(sketch, "E118.filletArc", {"start": v(-146.78, 84.5) * mm, "mid": v(-146.37, 83.53) * mm, "end": v(-145.4, 83.12) * mm});
            skCircle(sketch, "E119", {"center": v(116, 90.4) * mm, "radius": 1.6 * mm});
            skCircle(sketch, "E120", {"center": v(138, 90.4) * mm, "radius": 1.6 * mm});
            skLineSegment(sketch, "E121.bottom", {"start": v(121, 97.18) * mm, "end": v(133, 97.18) * mm});
            skLineSegment(sketch, "E121.top", {"start": v(121, 83.62) * mm, "end": v(133, 83.62) * mm});
            skLineSegment(sketch, "E121.left", {"start": v(119.73, 95.9) * mm, "end": v(119.73, 84.9) * mm});
            skLineSegment(sketch, "E121.right", {"start": v(134.28, 95.9) * mm, "end": v(134.28, 84.9) * mm});
            skPoint(sketch, "E122.visualSharp", {"position": v(119.73, 97.18) * mm});
            skArc(sketch, "E122.filletArc", {"start": v(121, 97.18) * mm, "mid": v(120.1, 96.8) * mm, "end": v(119.73, 95.9) * mm});
            skPoint(sketch, "E123.visualSharp", {"position": v(134.28, 97.18) * mm});
            skArc(sketch, "E123.filletArc", {"start": v(134.28, 95.9) * mm, "mid": v(133.9, 96.8) * mm, "end": v(133, 97.18) * mm});
            skPoint(sketch, "E124.visualSharp", {"position": v(134.28, 83.62) * mm});
            skArc(sketch, "E124.filletArc", {"start": v(133, 83.62) * mm, "mid": v(133.9, 84) * mm, "end": v(134.28, 84.9) * mm});
            skPoint(sketch, "E125.visualSharp", {"position": v(119.73, 83.62) * mm});
            skArc(sketch, "E125.filletArc", {"start": v(119.73, 84.9) * mm, "mid": v(120.1, 84) * mm, "end": v(121, 83.62) * mm});
            skPoint(sketch, "E126.center.orphan", {"position": v(0, -99.8) * mm});
            skLineSegment(sketch, "E127.bottom", {"start": v(-7.85, -93.45) * mm, "end": v(7.85, -93.45) * mm});
            skLineSegment(sketch, "E127.top", {"start": v(-7.85, -106.15) * mm, "end": v(7.85, -106.15) * mm});
            skLineSegment(sketch, "E127.left", {"start": v(-7.85, -93.45) * mm, "end": v(-7.85, -106.15) * mm});
            skLineSegment(sketch, "E127.right", {"start": v(7.85, -93.45) * mm, "end": v(7.85, -106.15) * mm});
            skPoint(sketch, "E128.center.orphan", {"position": v(150.5, 90.4) * mm});
            skLineSegment(sketch, "E129.MirrorCS", {"start": v(150.35, 85.95) * mm, "end": v(150.65, 85.95) * mm});
            skArc(sketch, "E130.MirrorCS", {"start": v(150.35, 85.95) * mm, "mid": v(147.3, 87.2) * mm, "end": v(146.05, 90.25) * mm});
            skArc(sketch, "E131.MirrorCS", {"start": v(154.95, 90.25) * mm, "mid": v(153.7, 87.2) * mm, "end": v(150.65, 85.95) * mm});
            skLineSegment(sketch, "E132.MirrorCS", {"start": v(146.05, 97.35) * mm, "end": v(154.95, 97.35) * mm});
            skLineSegment(sketch, "E133.MirrorCS", {"start": v(146.05, 90.25) * mm, "end": v(146.05, 97.35) * mm});
            skCircle(sketch, "E134.MirrorC", {"center": v(150.5, 99.4) * mm, "radius": 1.3 * mm});
            skLineSegment(sketch, "E135.MirrorCS", {"start": v(154.95, 90.25) * mm, "end": v(154.95, 97.35) * mm});
            skCircle(sketch, "E136.MirrorC", {"center": v(150.5, 83.9) * mm, "radius": 1.3 * mm});
            skSolve(sketch);
        }
        {
            var Q0;
            Q0 = qSketchRegion(id + "F0", true);
            extrude(context, id + "F1", {"entities" : qUnion([Q0]), "depth" : 3 * mm});
        }
    });
